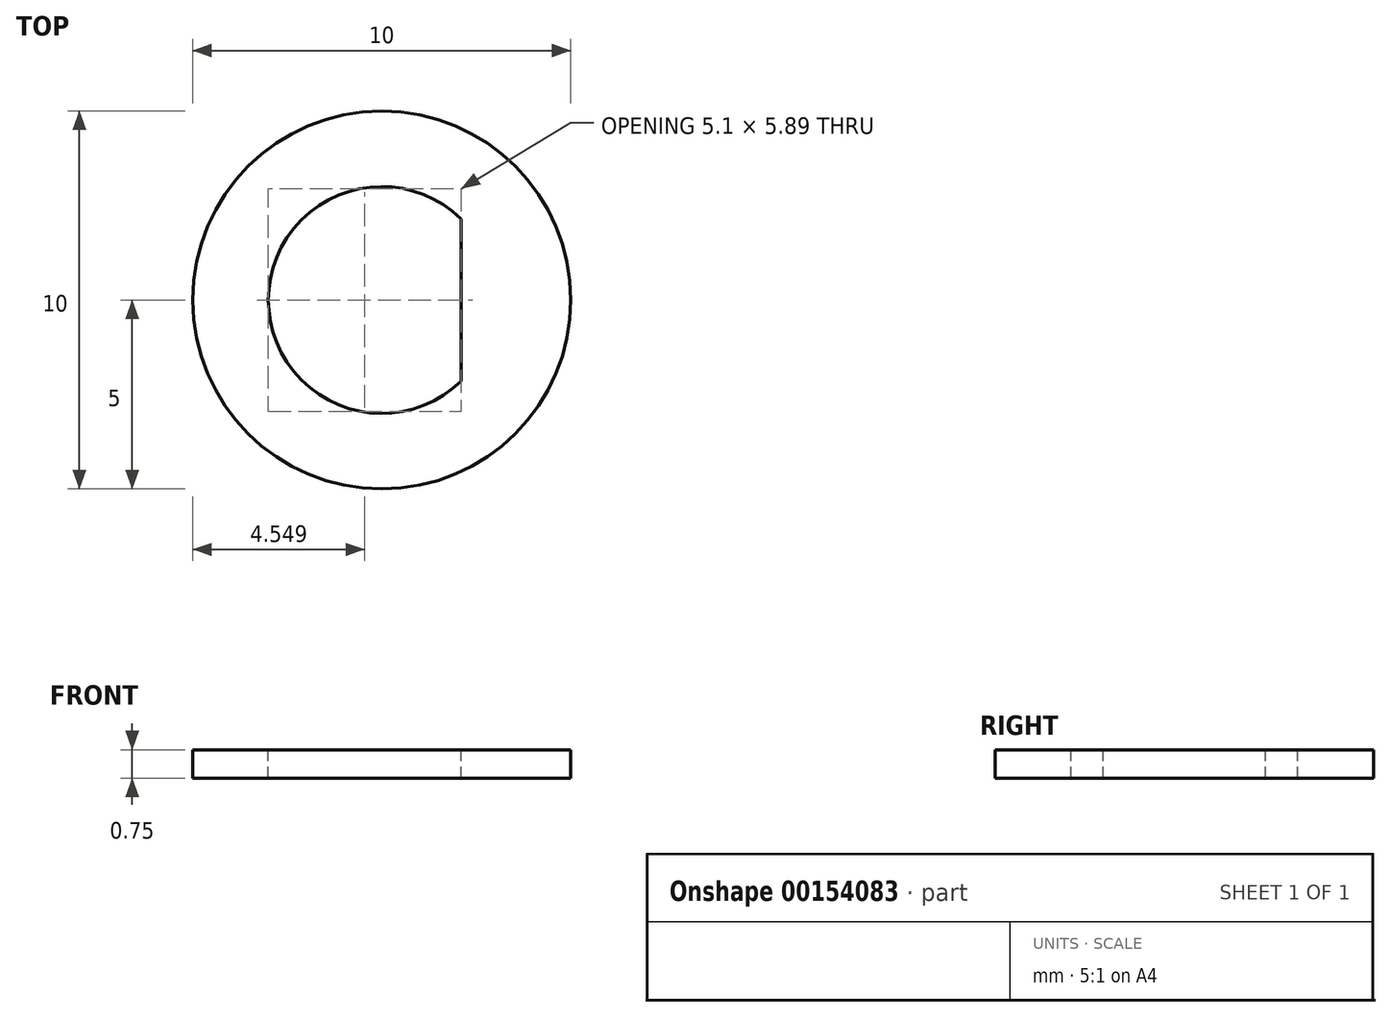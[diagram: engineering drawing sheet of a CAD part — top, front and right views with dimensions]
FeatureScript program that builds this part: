
annotation { "Feature Type Name" : "Feature", "Feature Type Description" : "" }
export const myFeature = defineFeature(function(context is Context, id is Id, definition is map)
    precondition{}
    {
        {
            var Q0;
            Q0=qCreatedBy(makeId("Top.planeOp"),FACE);
            var sketch = newSketch(context, id + "F0", { "sketchPlane" : qUnion([Q0])});
            skCircle(sketch, "E0", {"center": v(0, 0) * mm, "radius": 5 * mm});
            skSolve(sketch);
        }
        {
            var Q0;
            Q0=makeQuery(id+"F0.imprint","IMPRINT",FACE,{"disambiguationData":[TD([[makeQuery(id+"F0.imprint","IMPRINT",EDGE,{"derivedFrom":sQuery(id+"F0.wireOp",EDGE,"E0")}),1.0]])]});
            extrude(context, id + "F1", {"entities" : qUnion([Q0]), "oppositeDirection" : true, "depth" : 0.75 * mm});
        }
        {
            var Q0;
            Q0=qCreatedBy(makeId("Top.planeOp"),FACE);
            var sketch = newSketch(context, id + "F2", { "sketchPlane" : qUnion([Q0])});
            skArc(sketch, "E1", {"start": v(2.1, 2.14) * mm, "mid": v(-3, 0) * mm, "end": v(2.1, -2.14) * mm});
            skLineSegment(sketch, "E2", {"start": v(2.1, 2.14) * mm, "end": v(2.1, -2.14) * mm});
            skSolve(sketch);
        }
        {
            var Q0;
            Q0 = qSketchRegion(id + "F2", true);
            extrude(context, id + "F3", {"entities" : qUnion([Q0]), "operationType" : NewBodyOperationType.REMOVE, "endBound" : BoundingType.THROUGH_ALL, "oppositeDirection" : true, "depth" : 25 * mm});
        }
    });
